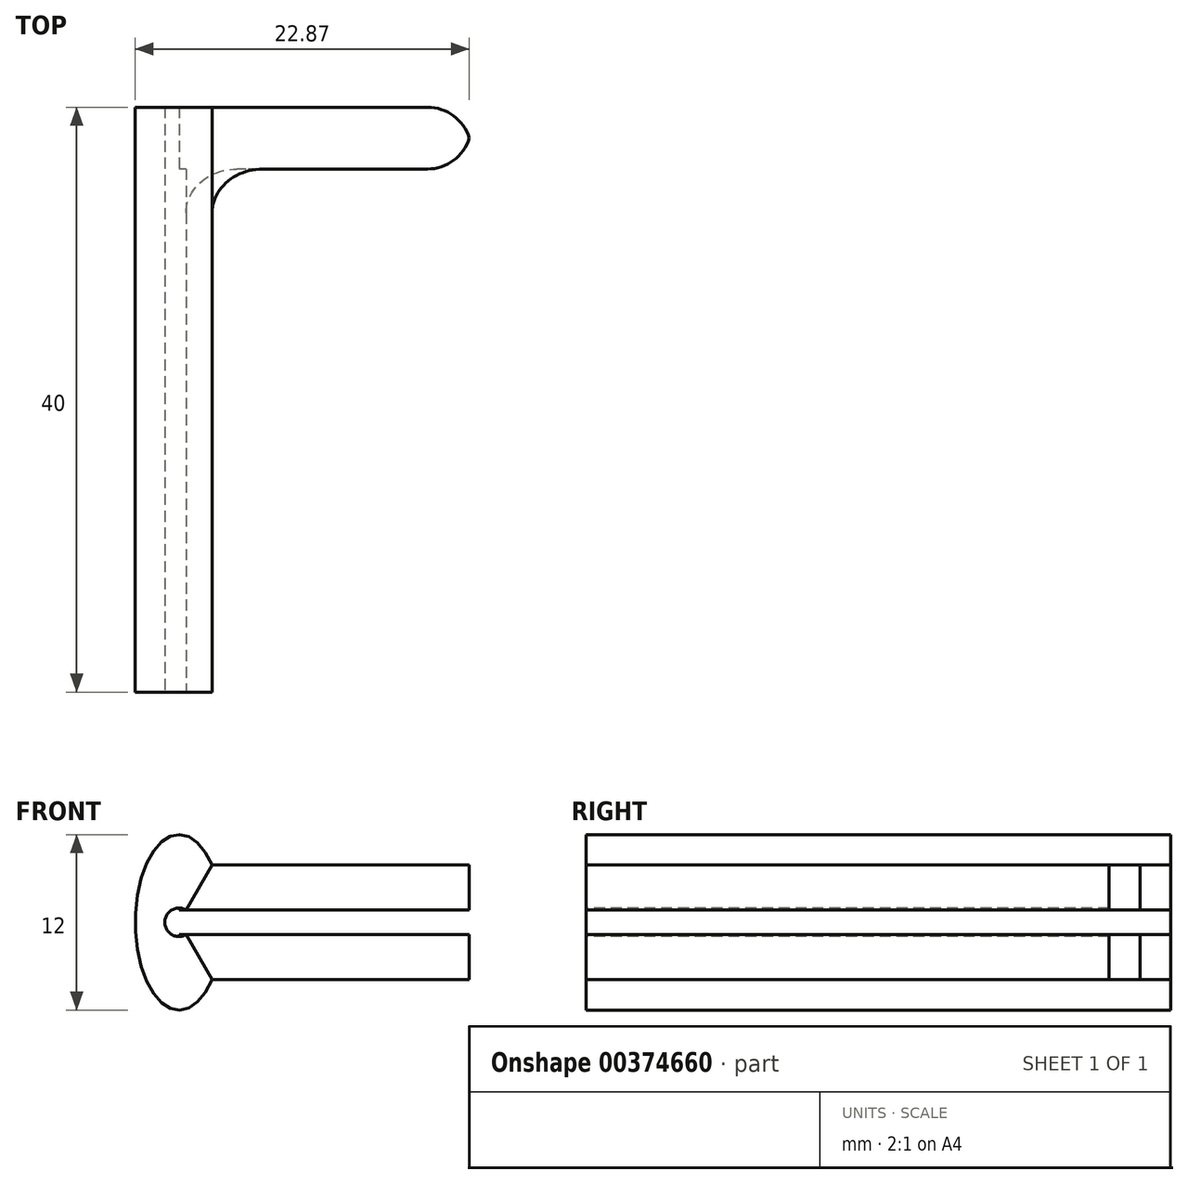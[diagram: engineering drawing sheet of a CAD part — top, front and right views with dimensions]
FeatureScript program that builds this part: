
annotation { "Feature Type Name" : "Feature", "Feature Type Description" : "" }
export const myFeature = defineFeature(function(context is Context, id is Id, definition is map)
    precondition{}
    {
        {
            var Q0;
            Q0=qCreatedBy(makeId("Front.planeOp"),FACE);
            var sketch = newSketch(context, id + "F0", { "sketchPlane" : qUnion([Q0])});
            skArc(sketch, "E0", {"start": v(0.49, 0.84) * mm, "mid": v(-0.97, 0) * mm, "end": v(0.49, -0.84) * mm});
            skLineSegment(sketch, "E1", {"start": v(0.49, 0.84) * mm, "end": v(2.27, 3.93) * mm});
            skLineSegment(sketch, "E2", {"start": v(0.49, -0.84) * mm, "end": v(2.27, -3.93) * mm});
            skEllipticalArc(sketch, "E3", {});
            const initialGuessF0  = {"E3": [0, 0, -1, 0, 0.003, 0.006, 3.8553170325345567, 2.4278682746450277]};
            skSetInitialGuess(sketch, initialGuessF0);
            skSolve(sketch);
        }
        {
            var Q0;
            Q0=qCreatedBy(makeId("Top.planeOp"),FACE);
            var sketch = newSketch(context, id + "F1", { "sketchPlane" : qUnion([Q0])});
            skLineSegment(sketch, "E4", {"start": v(0, 0) * mm, "end": v(0, 37) * mm});
            skArc(sketch, "E5", {"start": v(0, 37) * mm, "mid": v(0.64, 38.56) * mm, "end": v(2.2, 39.2) * mm});
            skLineSegment(sketch, "E6", {"start": v(2.2, 39.2) * mm, "end": v(12.2, 39.2) * mm});
            skSolve(sketch);
        }
        {
            var Q0;
            Q0=qSketchRegion(id+"F0",true);
            extrude(context, id + "F2", {"entities" : qUnion([Q0]), "oppositeDirection" : true, "depth" : 40 * mm});
        }
        {
            var Q0;
            Q0=makeQuery(id+"F2.opExtrude","CAP_FACE",FACE,{"disambiguationData":[OSD([sQuery(id+"F0.wireOp",EDGE,"hwYrKBq2-fvbr-EDF6-C3oE-UpZH6pCpzC1p"),sQuery(id+"F0.wireOp",EDGE,"E0"),sQuery(id+"F0.wireOp",EDGE,"E1"),sQuery(id+"F0.wireOp",EDGE,"E2")])],"isStart":false});
            var sketch = newSketch(context, id + "F3", { "sketchPlane" : qUnion([Q0])});
            skEllipse(sketch, "E7", {"center": v(0, 0) * mm, "majorRadius": 3 * mm, "minorRadius": 6 * mm, "majorAxis": v(1, 0)});
            skSolve(sketch);
        }
        {
            var Q0;
            Q0=qCreatedBy(makeId("Right.planeOp"),FACE);
            var sketch = newSketch(context, id + "F4", { "sketchPlane" : qUnion([Q0])});
            skLineSegment(sketch, "E8.bottom", {"start": v(40, 0.84) * mm, "end": v(35.78, 0.84) * mm});
            skLineSegment(sketch, "E8.top", {"start": v(40, 3.93) * mm, "end": v(35.78, 3.93) * mm});
            skLineSegment(sketch, "E8.left", {"start": v(40, 0.84) * mm, "end": v(40, 3.93) * mm});
            skLineSegment(sketch, "E8.right", {"start": v(35.78, 0.84) * mm, "end": v(35.78, 3.93) * mm});
            skPoint(sketch, "E9.firstSnap0", {"position": v(35.78, 2.39) * mm});
            skLineSegment(sketch, "E9.bottom", {"start": v(35.78, -0.84) * mm, "end": v(40, -0.84) * mm});
            skLineSegment(sketch, "E9.top", {"start": v(35.78, -3.93) * mm, "end": v(40, -3.93) * mm});
            skLineSegment(sketch, "E9.left", {"start": v(35.78, -0.84) * mm, "end": v(35.78, -3.93) * mm});
            skLineSegment(sketch, "E9.right", {"start": v(40, -0.84) * mm, "end": v(40, -3.93) * mm});
            skSolve(sketch);
        }
        {
            var Q0;
            Q0=qSketchRegion(id+"F4",true);
            extrude(context, id + "F5", {"entities" : qUnion([Q0]), "operationType" : NewBodyOperationType.ADD, "depth" : 20 * mm});
        }
        {
            var Q0;
            Q0=makeQuery(id+"F5.boolean.opBoolean","INTERSECT",EDGE,{"derivedFrom":[makeQuery(id+"F2.opExtrude","SWEPT_FACE",FACE,{"disambiguationData":[OSD([sQuery(id+"F0.wireOp",EDGE,"E1")])]}),makeQuery(id+"F5.opExtrude","SWEPT_FACE",FACE,{"disambiguationData":[OSD([sQuery(id+"F4.wireOp",EDGE,"E8.right")])]})]});
            var Q1;
            Q1=makeQuery(id+"F5.boolean.opBoolean","INTERSECT",EDGE,{"derivedFrom":[makeQuery(id+"F2.opExtrude","SWEPT_FACE",FACE,{"disambiguationData":[OSD([sQuery(id+"F0.wireOp",EDGE,"E2")])]}),makeQuery(id+"F5.opExtrude","SWEPT_FACE",FACE,{"disambiguationData":[OSD([sQuery(id+"F4.wireOp",EDGE,"E9.left")])]})]});
            var Q2;
            Q2=makeQuery(id+"F5.opExtrude","CAP_EDGE",EDGE,{"disambiguationData":[OSD([sQuery(id+"F4.wireOp",EDGE,"E8.right")])],"isStart":false});
            var Q3;
            Q3=makeQuery(id+"F5.opExtrude","CAP_EDGE",EDGE,{"disambiguationData":[OSD([sQuery(id+"F4.wireOp",EDGE,"E9.left")])],"isStart":false});
            var Q4;
            Q4=makeQuery(id+"F5.opExtrude","CAP_EDGE",EDGE,{"disambiguationData":[OSD([sQuery(id+"F4.wireOp",EDGE,"E9.right")])],"isStart":false});
            var Q5;
            Q5=makeQuery(id+"F5.opExtrude","CAP_EDGE",EDGE,{"disambiguationData":[OSD([sQuery(id+"F4.wireOp",EDGE,"E8.left")])],"isStart":false});
            fillet(context, id + "F6", {"entities" : qUnion([Q0, Q1, Q2, Q3, Q4, Q5]), "radius" : 3 * mm, "tangentPropagation" : true, "allowEdgeOverflow" : false});
        }
    });
